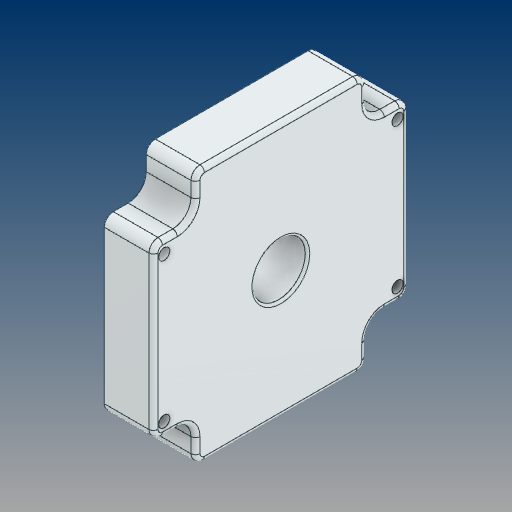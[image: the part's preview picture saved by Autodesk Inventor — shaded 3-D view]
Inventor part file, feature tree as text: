
AUTODESK INVENTOR PART (.ipt)
format: ipt  version: 2021 (Build 250183000, 183)  size: 176,128 bytes
history: native  units: mm
features: fillet x1
ambient origin geometry x8: Origin, YZ Plane, XZ Plane, XY Plane, X Axis, Y Axis, Z Axis, Center Point
bodies: Solid1 (feature_tree)
feature tree (1):
  fillet  "Fillet2"  [1 undecoded]
note: 1 required parameter value undecoded (feature->parameter linkage not recoverable at this tier; creation-order binding heuristic only, values carry confidence <= 0.55)
